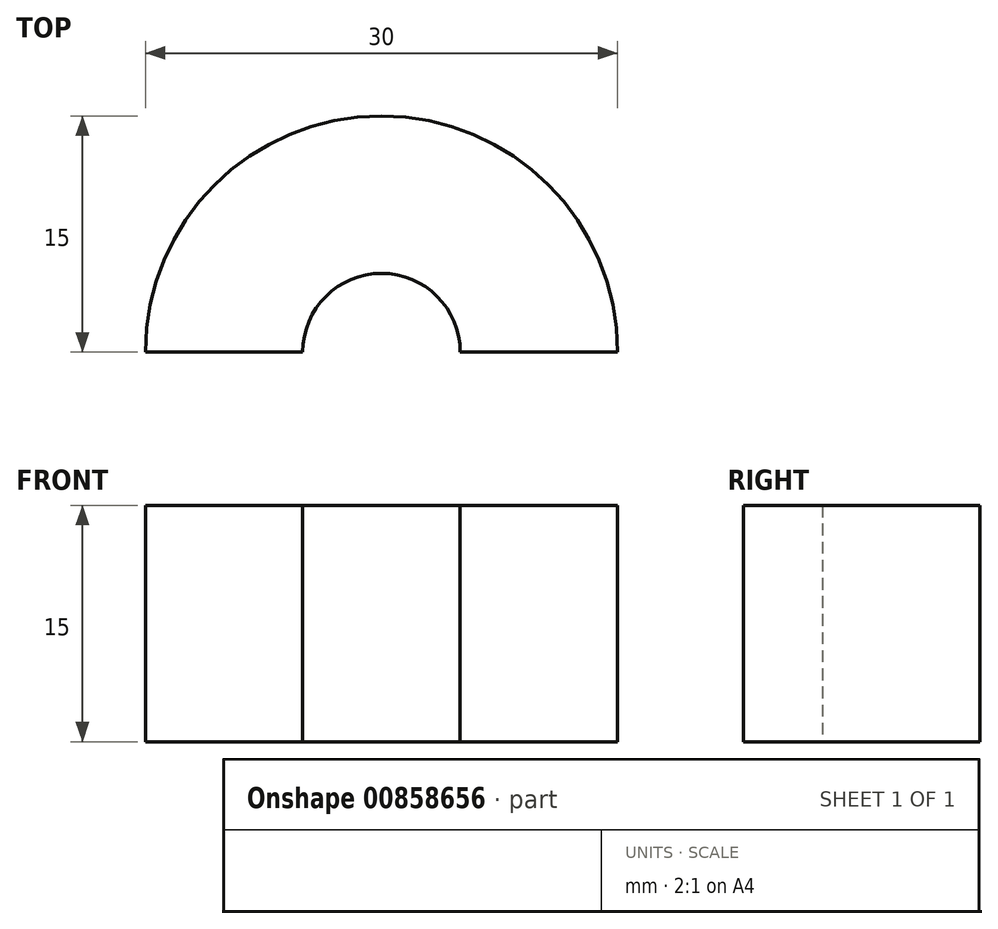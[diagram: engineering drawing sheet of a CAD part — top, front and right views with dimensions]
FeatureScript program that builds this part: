
annotation { "Feature Type Name" : "Feature", "Feature Type Description" : "" }
export const myFeature = defineFeature(function(context is Context, id is Id, definition is map)
    precondition{}
    {
        {
            var Q0;
            Q0=qCreatedBy(makeId("Top.planeOp"),FACE);
            var sketch = newSketch(context, id + "F0", { "sketchPlane" : qUnion([Q0])});
            skLineSegment(sketch, "E0", {"start": v(0, 0) * mm, "end": v(10, 0) * mm});
            skArc(sketch, "E1", {"start": v(20, 0) * mm, "mid": v(15, 5) * mm, "end": v(10, 0) * mm});
            skLineSegment(sketch, "E2", {"start": v(20, 0) * mm, "end": v(30, 0) * mm});
            skArc(sketch, "E3", {"start": v(30, 0) * mm, "mid": v(15, 15) * mm, "end": v(0, 0) * mm});
            skSolve(sketch);
        }
        {
            var Q0;
            Q0=makeQuery(id+"F0.imprint","IMPRINT",FACE,{"disambiguationData":[TD([[makeQuery(id+"F0.imprint","IMPRINT",EDGE,{"derivedFrom":sQuery(id+"F0.wireOp",EDGE,"E0")}),1.0]])]});
            extrude(context, id + "F1", {"entities" : qUnion([Q0]), "depth" : 15 * mm, "offsetDistance" : 25 * mm});
        }
    });
